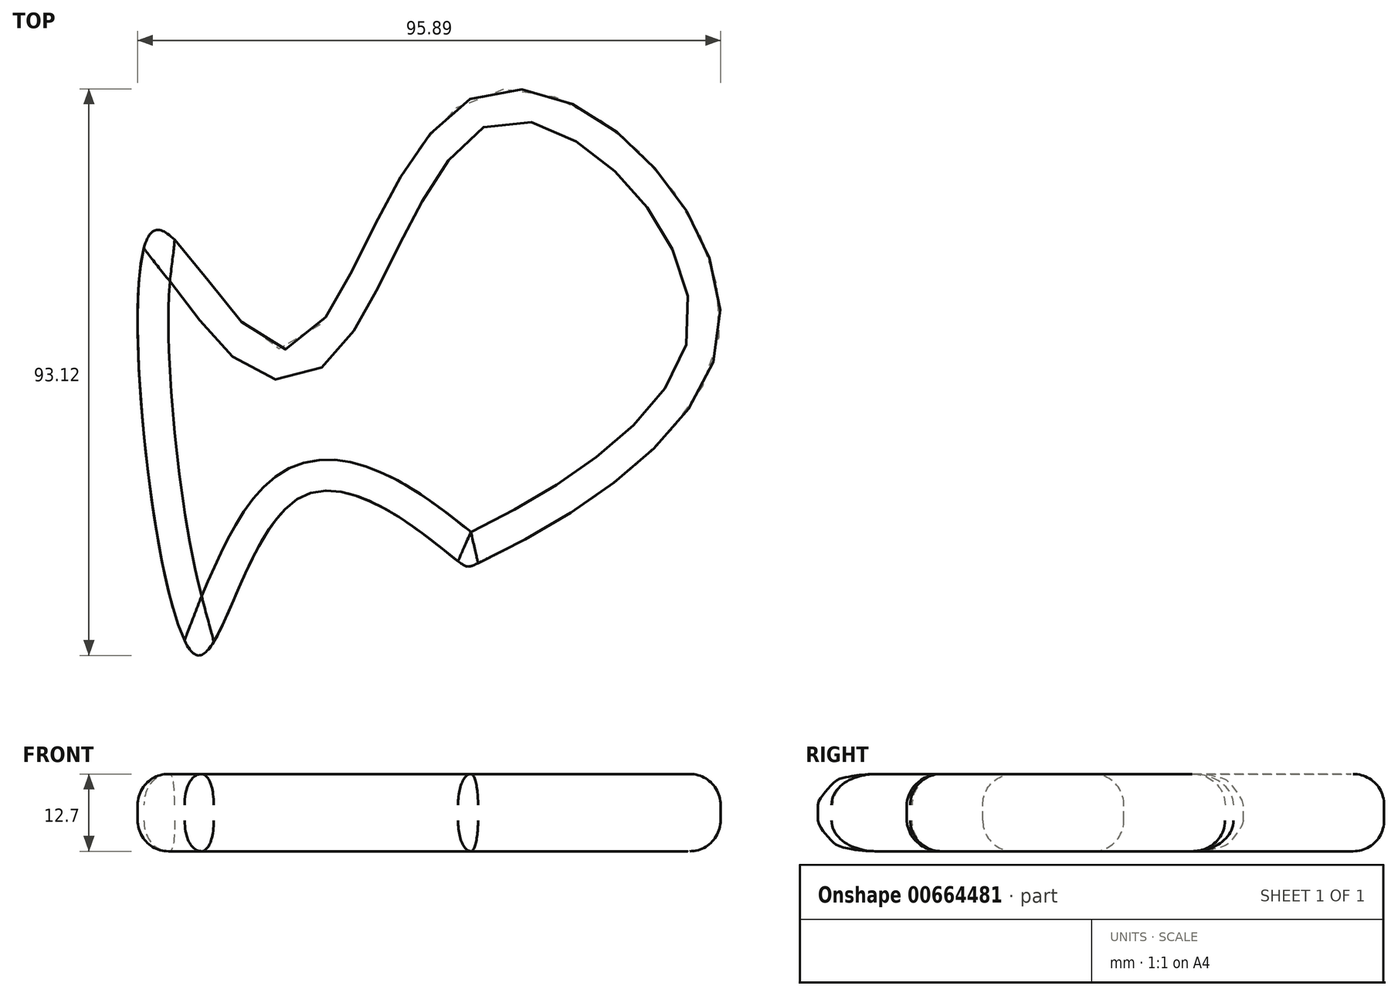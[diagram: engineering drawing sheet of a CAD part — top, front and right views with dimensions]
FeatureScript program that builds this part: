
annotation { "Feature Type Name" : "Feature", "Feature Type Description" : "" }
export const myFeature = defineFeature(function(context is Context, id is Id, definition is map)
    precondition{}
    {
        {
            var Q0;
            Q0=qCreatedBy(makeId("Top.planeOp"),FACE);
            var sketch = newSketch(context, id + "F0", { "sketchPlane" : qUnion([Q0])});
            skFitSpline(sketch, "E0", {"points": [v(0, 0) * mm, v(39.56, 37.47) * mm, v(0, 76.88) * mm, v(-32.4, 35.08) * mm, v(-53.59, 54.48) * mm, v(-46.72, -15.08) * mm, v(-29.1, 10.9) * mm, v(-3.13, 0) * mm, v(0, 0) * mm]});
            skSolve(sketch);
        }
        {
            var Q0;
            Q0=makeQuery(id+"F0.imprint","IMPRINT",FACE,{"disambiguationData":[TD([[makeQuery(id+"F0.imprint","IMPRINT",EDGE,{"derivedFrom":sQuery(id+"F0.wireOp",EDGE,"E0")}),1.0]])]});
            extrude(context, id + "F1", {"entities" : qUnion([Q0]), "depth" : 12.7 * mm, "offsetDistance" : 25.4 * mm});
        }
        {
            var Q0;
            Q0=makeQuery(id+"F1.opExtrude","CAP_EDGE",EDGE,{"disambiguationData":[OSD([sQuery(id+"F0.wireOp",EDGE,"E0")])],"isStart":false});
            fillet(context, id + "F2", {"entities" : qUnion([Q0]), "tangentPropagation" : true, "radius" : 5.08 * mm, "defaultsChanged" : false, "vertexSettings" : [], "allowEdgeOverflow" : false});
        }
        {
            var Q0;
            Q0=makeQuery(id+"F1.opExtrude","CAP_EDGE",EDGE,{"disambiguationData":[OSD([sQuery(id+"F0.wireOp",EDGE,"E0")])],"isStart":true});
            fillet(context, id + "F3", {"entities" : qUnion([Q0]), "tangentPropagation" : true, "radius" : 5.08 * mm, "defaultsChanged" : false, "vertexSettings" : [], "allowEdgeOverflow" : false});
        }
    });
